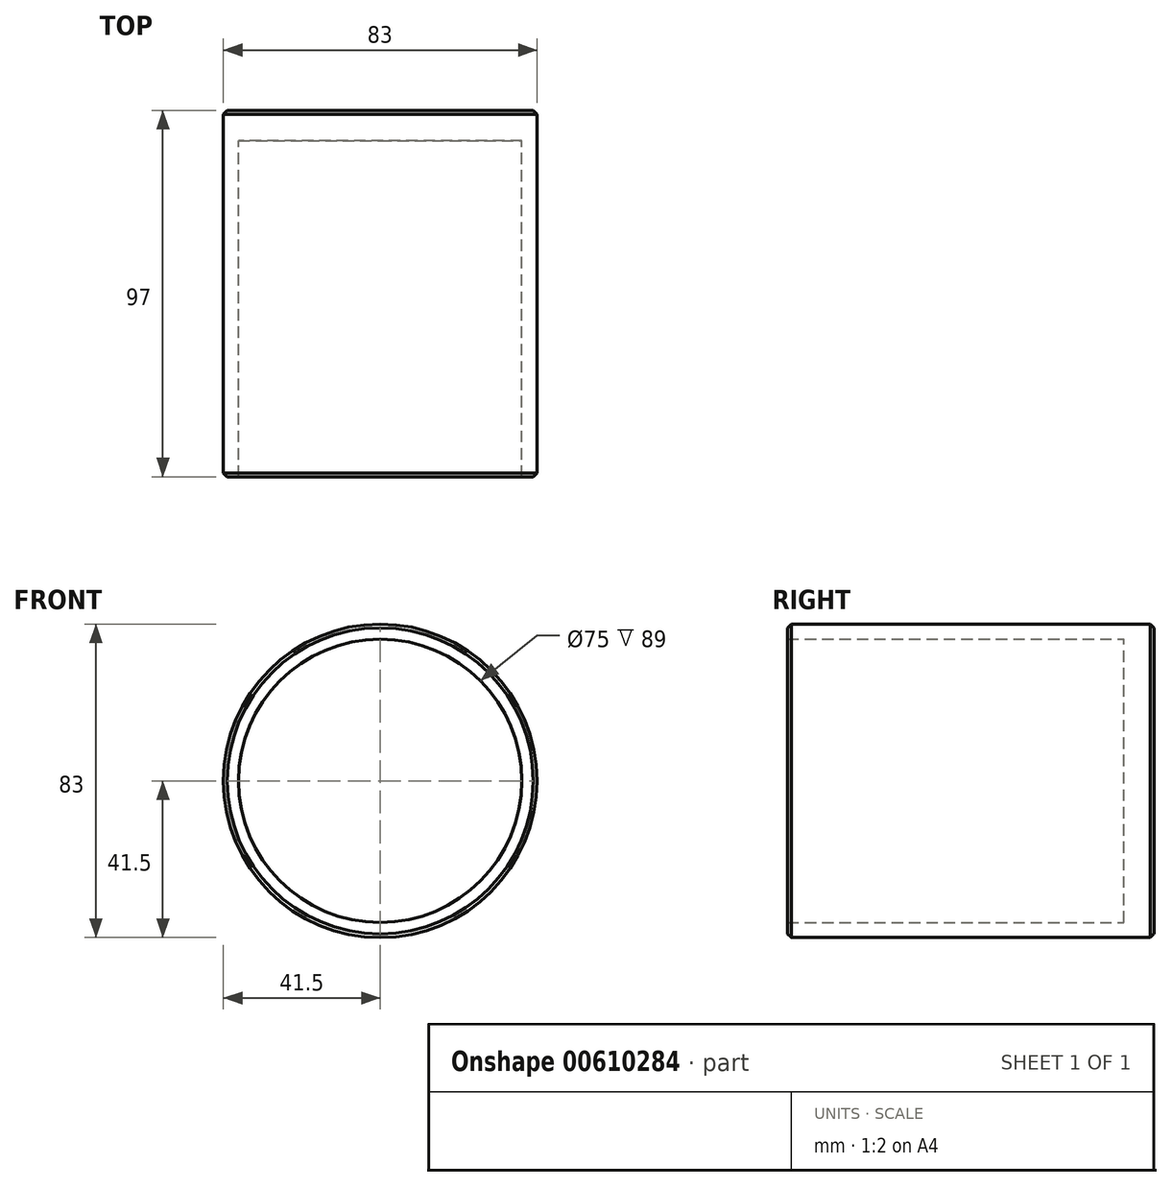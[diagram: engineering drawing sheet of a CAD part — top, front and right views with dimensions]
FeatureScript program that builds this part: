
annotation { "Feature Type Name" : "Feature", "Feature Type Description" : "" }
export const myFeature = defineFeature(function(context is Context, id is Id, definition is map)
    precondition{}
    {
        {
            var Q0;
            Q0=qCreatedBy(makeId("Front.planeOp"),FACE);
            var sketch = newSketch(context, id + "F0", { "sketchPlane" : qUnion([Q0])});
            skCircle(sketch, "E0", {"center": v(0, 0) * mm, "radius": 41.5 * mm});
            skCircle(sketch, "E1", {"center": v(0, 0) * mm, "radius": 37.5 * mm});
            skSolve(sketch);
        }
        {
            var Q0;
            Q0=makeQuery(id+"F0.imprint","IMPRINT",FACE,{"disambiguationData":[TD([[makeQuery(id+"F0.imprint","IMPRINT",EDGE,{"derivedFrom":sQuery(id+"F0.wireOp",EDGE,"E0")}),1.0]])]});
            extrude(context, id + "F1", {"entities" : qUnion([Q0]), "depth" : 97 * mm, "offsetDistance" : 25 * mm});
        }
        {
            var Q0;
            Q0=makeQuery(id+"F0.imprint","IMPRINT",FACE,{"disambiguationData":[TD([[makeQuery(id+"F0.imprint","IMPRINT",EDGE,{"derivedFrom":sQuery(id+"F0.wireOp",EDGE,"E1")}),1.0]])]});
            extrude(context, id + "F2", {"entities" : qUnion([Q0]), "operationType" : NewBodyOperationType.ADD, "depth" : 8 * mm, "offsetDistance" : 25 * mm});
        }
        {
            var Q0;
            Q0=makeQuery(id+"F1.opExtrude","SWEPT_FACE",FACE,{"disambiguationData":[OSD([sQuery(id+"F0.wireOp",EDGE,"E0")])]});
            chamfer(context, id + "F3", {"entities" : qUnion([Q0]), "width" : 1 * mm, "tangentPropagation" : true});
        }
    });
